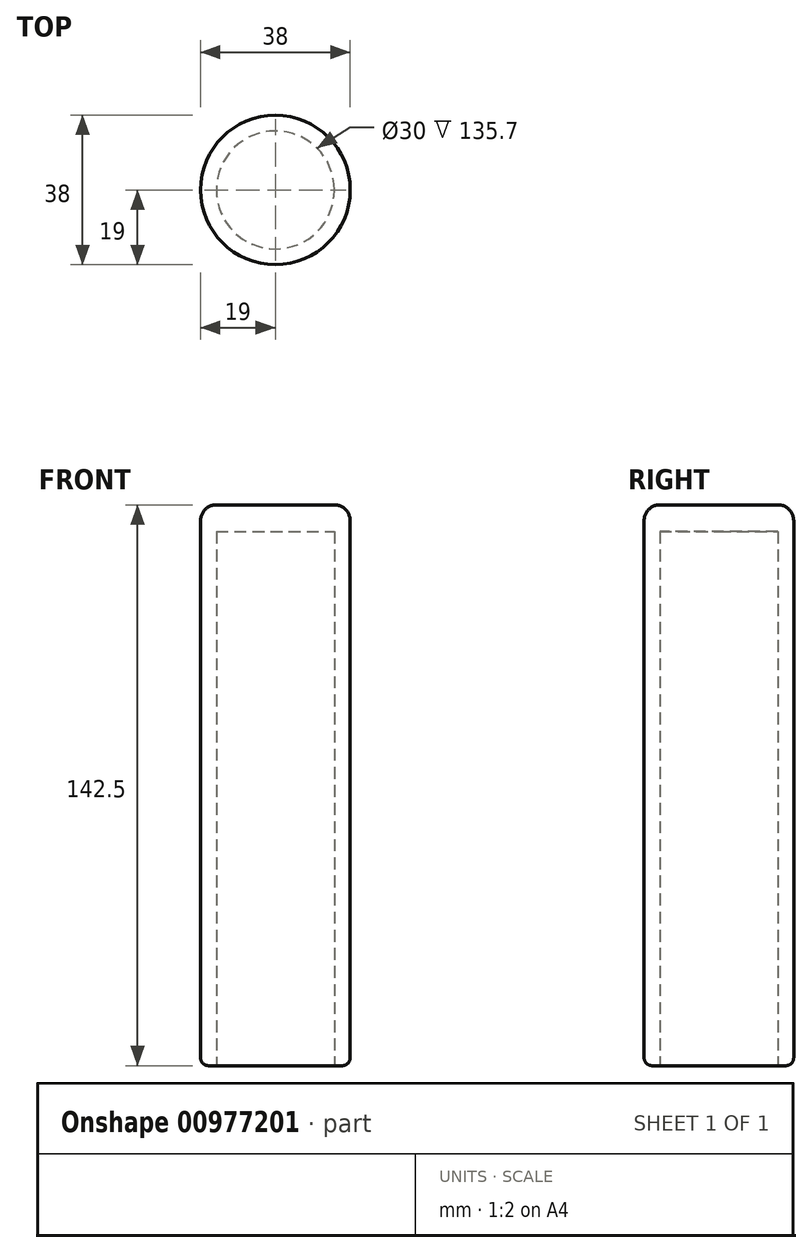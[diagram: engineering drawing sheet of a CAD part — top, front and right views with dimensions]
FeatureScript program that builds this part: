
annotation { "Feature Type Name" : "Feature", "Feature Type Description" : "" }
export const myFeature = defineFeature(function(context is Context, id is Id, definition is map)
    precondition{}
    {
        {
            var Q0;
            Q0=qCreatedBy(makeId("Top.planeOp"),FACE);
            var sketch = newSketch(context, id + "F0", { "sketchPlane" : qUnion([Q0])});
            skCircle(sketch, "E0", {"center": v(0, 0) * mm, "radius": 19 * mm});
            skSolve(sketch);
        }
        {
            var Q0;
            Q0=makeQuery(id+"F0.imprint","IMPRINT",FACE,{"disambiguationData":[TD([[makeQuery(id+"F0.imprint","IMPRINT",EDGE,{"derivedFrom":sQuery(id+"F0.wireOp",EDGE,"E0")}),1.0]])]});
            extrude(context, id + "F1", {"entities" : qUnion([Q0]), "depth" : 135 * mm, "offsetDistance" : 25 * mm});
        }
        {
            var Q0;
            Q0=makeQuery(id+"F1.opExtrude","CAP_EDGE",EDGE,{"disambiguationData":[OSD([sQuery(id+"F0.wireOp",EDGE,"E0")])],"isStart":false});
            fillet(context, id + "F2", {"entities" : qUnion([Q0]), "radius" : 4 * mm, "tangentPropagation" : true, "allowEdgeOverflow" : false});
        }
        {
            var Q0;
            Q0=qCreatedBy(makeId("Top.planeOp"),FACE);
            var sketch = newSketch(context, id + "F3", { "sketchPlane" : qUnion([Q0])});
            skCircle(sketch, "E1.0", {"center": v(0, 0) * mm, "radius": 19 * mm});
            skSolve(sketch);
        }
        {
            var Q0;
            Q0=makeQuery(id+"F3.imprint","IMPRINT",FACE,{"disambiguationData":[TD([[makeQuery(id+"F3.imprint","IMPRINT",EDGE,{"derivedFrom":sQuery(id+"F3.wireOp",EDGE,"E1.0")}),1.0]])]});
            extrude(context, id + "F4", {"entities" : qUnion([Q0]), "operationType" : NewBodyOperationType.ADD, "oppositeDirection" : true, "depth" : 7.5 * mm, "offsetDistance" : 25 * mm});
        }
        {
            var Q0;
            Q0=makeQuery(id+"F4.opExtrude","CAP_FACE",FACE,{"disambiguationData":[OSD([sQuery(id+"F3.wireOp",EDGE,"E1.0")])],"isStart":false});
            var sketch = newSketch(context, id + "F5", { "sketchPlane" : qUnion([Q0])});
            skCircle(sketch, "E2", {"center": v(0, 0) * mm, "radius": 15 * mm});
            skSolve(sketch);
        }
        {
            var Q0;
            Q0=makeQuery(id+"F5.imprint","IMPRINT",FACE,{"disambiguationData":[TD([[makeQuery(id+"F5.imprint","IMPRINT",EDGE,{"derivedFrom":sQuery(id+"F5.wireOp",EDGE,"E2")}),1.0]])]});
            extrude(context, id + "F6", {"entities" : qUnion([Q0]), "operationType" : NewBodyOperationType.REMOVE, "oppositeDirection" : true, "depth" : 135.7 * mm, "offsetDistance" : 25 * mm});
        }
        {
            var Q0;
            Q0=makeQuery(id+"F4.opExtrude","CAP_EDGE",EDGE,{"disambiguationData":[OSD([sQuery(id+"F3.wireOp",EDGE,"E1.0")])],"isStart":false});
            fillet(context, id + "F7", {"entities" : qUnion([Q0]), "radius" : 2 * mm, "tangentPropagation" : true, "allowEdgeOverflow" : false});
        }
    });
